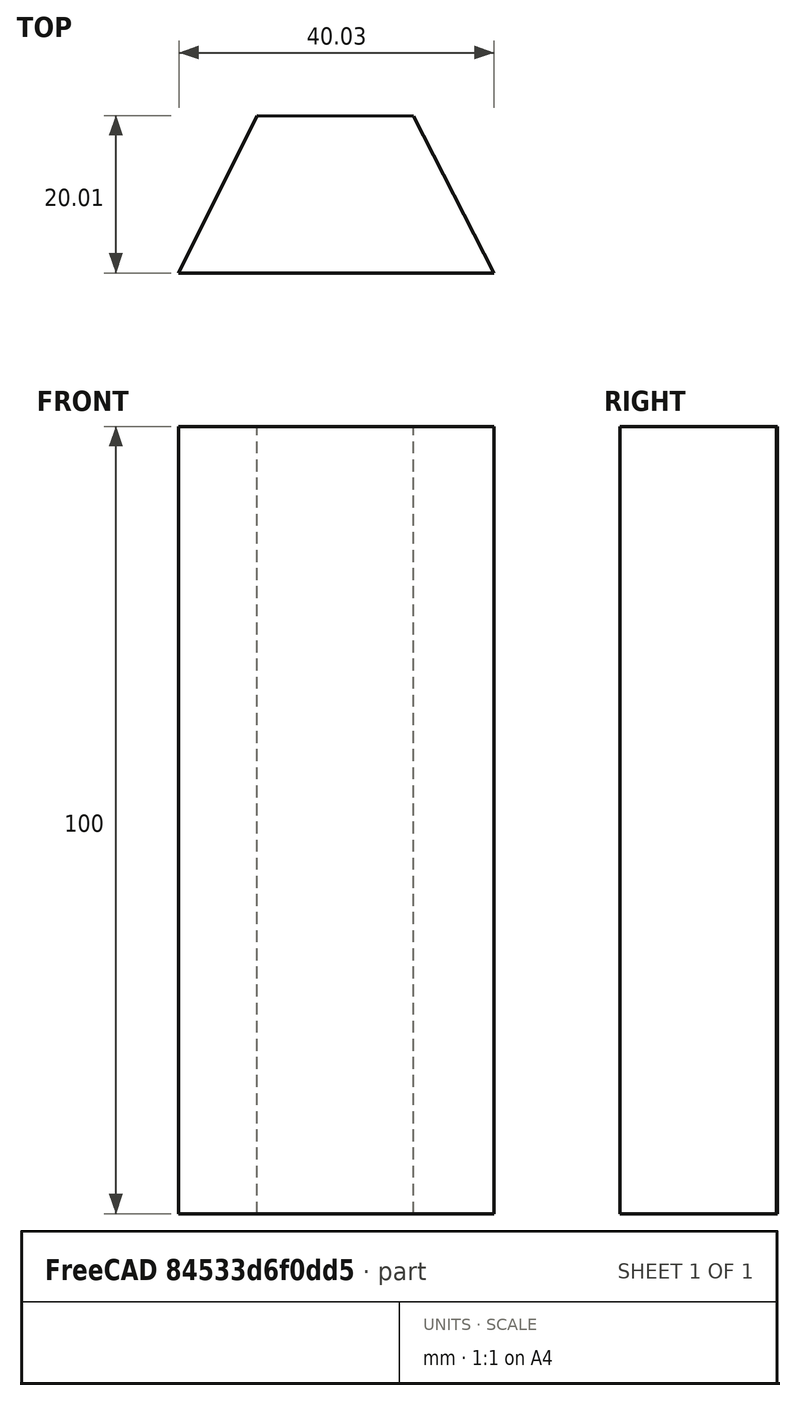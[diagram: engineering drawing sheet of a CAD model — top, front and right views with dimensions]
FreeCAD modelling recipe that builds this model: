
FCSTD DOCUMENT  (FreeCAD 0.21R33771 (Git))
Label: OJT1_T16P02_lingot
License: All rights reserved
LicenseURL: http://en.wikipedia.org/wiki/All_rights_reserved
objects: Sketcher::SketchObject×1, PartDesign::Pad×1, PartDesign::Body×1
note: 4 computed .brp shape members not serialized (recipe doc carries the construction recipe); baked Part::Feature solids carry a one-line shape summary decoded from their .brp

FEATURE [Sketcher::SketchObject] Sketch
  FullyConstrained = false
  MapMode = 5
  Support = -> [XY_Plane]
  sketch-geometry (4):
    g0: LineSegment StartX=-19.9111 StartY=0 StartZ=0 EndX=20.1245 EndY=0 EndZ=0
    g1: LineSegment StartX=20.1245 StartY=0 StartZ=0 EndX=9.93194 EndY=19.9134 EndZ=0
    g2: LineSegment StartX=9.93194 StartY=19.9134 StartZ=0 EndX=-9.99402 EndY=20.0052 EndZ=0
    g3: LineSegment StartX=-9.99402 StartY=20.0052 StartZ=0 EndX=-19.9111 EndY=0 EndZ=0
  constraints (4):
    c: Coincident(g0,g1)
    c: Coincident(g1,g2)
    c: Coincident(g2,g3)
    c: Coincident(g3,g0)
FEATURE [PartDesign::Pad] Pad
  Direction = (0,0,1)
  Length = 100
  Length2 = 10
  Profile = -> Sketch
  ReferenceAxis = -> Sketch [N_Axis]
  Type = 0
FEATURE [PartDesign::Body] Body
  Group = -> [Sketch,Pad]
  Origin = -> Origin
  Tip = -> Pad
